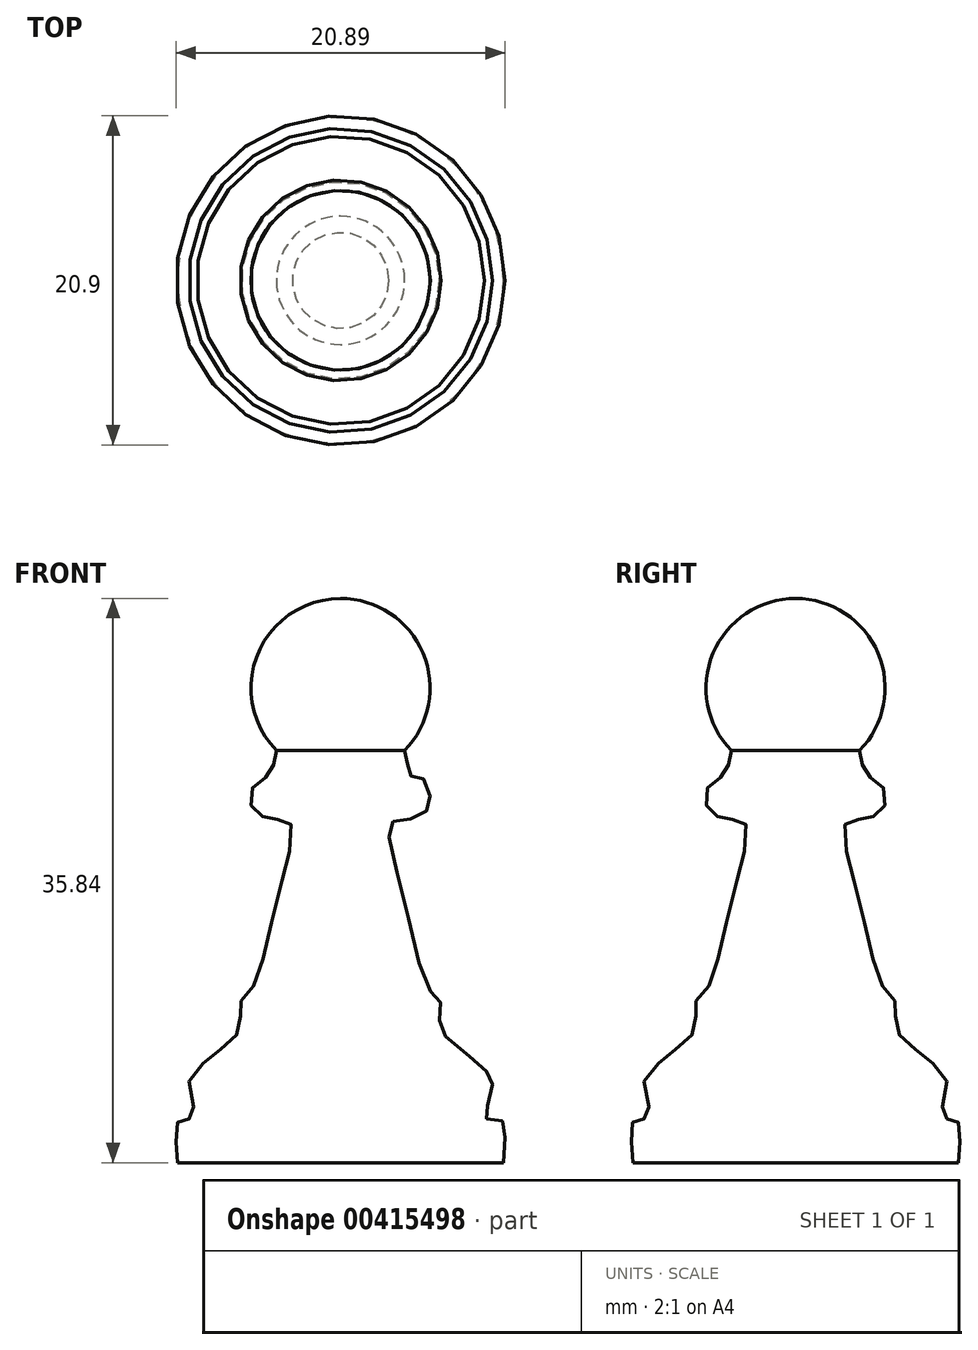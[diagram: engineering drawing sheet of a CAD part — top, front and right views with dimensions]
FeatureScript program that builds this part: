
annotation { "Feature Type Name" : "Feature", "Feature Type Description" : "" }
export const myFeature = defineFeature(function(context is Context, id is Id, definition is map)
    precondition{}
    {
        {
            var Q0;
            Q0=qCreatedBy(makeId("Front.planeOp"),FACE);
            var sketch = newSketch(context, id + "F0", { "sketchPlane" : qUnion([Q0])});
            skLineSegment(sketch, "E0", {"start": v(-17.76, -14.18) * mm, "end": v(12.24, -14.18) * mm, "construction": true});
            skArc(sketch, "E1", {"start": v(-1.27, 8.9) * mm, "mid": v(-6.51, 5.42) * mm, "end": v(-5.34, -0.76) * mm});
            skFitSpline(sketch, "E2", {"points": [v(-5.34, -0.76) * mm, v(-5.5, -1.44) * mm, v(-5.61, -2.04) * mm, v(-5.82, -2.43) * mm, v(-6.5, -2.54) * mm, v(-6.96, -3.6) * mm, v(-6.85, -4.45) * mm, v(-5.93, -5.05) * mm, v(-4.73, -5.23) * mm, v(-4.34, -5.68) * mm, v(-5.34, -10.4) * mm, v(-6.94, -15.99) * mm, v(-7.57, -16.61) * mm, v(-7.6, -17.7) * mm, v(-7.66, -18.57) * mm, v(-9.95, -20.58) * mm, v(-10.74, -21.42) * mm, v(-10.9, -22.22) * mm, v(-10.44, -23.86) * mm, v(-10.5, -24.13) * mm, v(-11.44, -24.23) * mm, v(-11.71, -24.83) * mm, v(-11.61, -26.94) * mm], "startDerivative": vector(-17.3, -14.12) * mm, "endDerivative": vector(3.14, -39.68) * mm});
            skLineSegment(sketch, "E3", {"start": v(-11.61, -26.94) * mm, "end": v(-1.27, -26.94) * mm});
            skLineSegment(sketch, "E4", {"start": v(-1.27, 3.2) * mm, "end": v(-1.27, -26.94) * mm});
            skLineSegment(sketch, "E5", {"start": v(-1.27, 8.9) * mm, "end": v(-1.27, 3.2) * mm});
            skSolve(sketch);
        }
        {
            var Q0;
            Q0=makeQuery(id+"F0.imprint","IMPRINT",FACE,{"disambiguationData":[TD([[makeQuery(id+"F0.imprint","IMPRINT",EDGE,{"derivedFrom":sQuery(id+"F0.wireOp",EDGE,"E1")}),1.0]])]});
            var Q1;
            Q1=sQuery(id+"F0.wireOp",EDGE,"E4");
            revolve(context, id + "F1", {"entities" : qUnion([Q0]), "axis" : qUnion([Q1]), "revolveType" : RevolveType.FULL});
        }
    });
